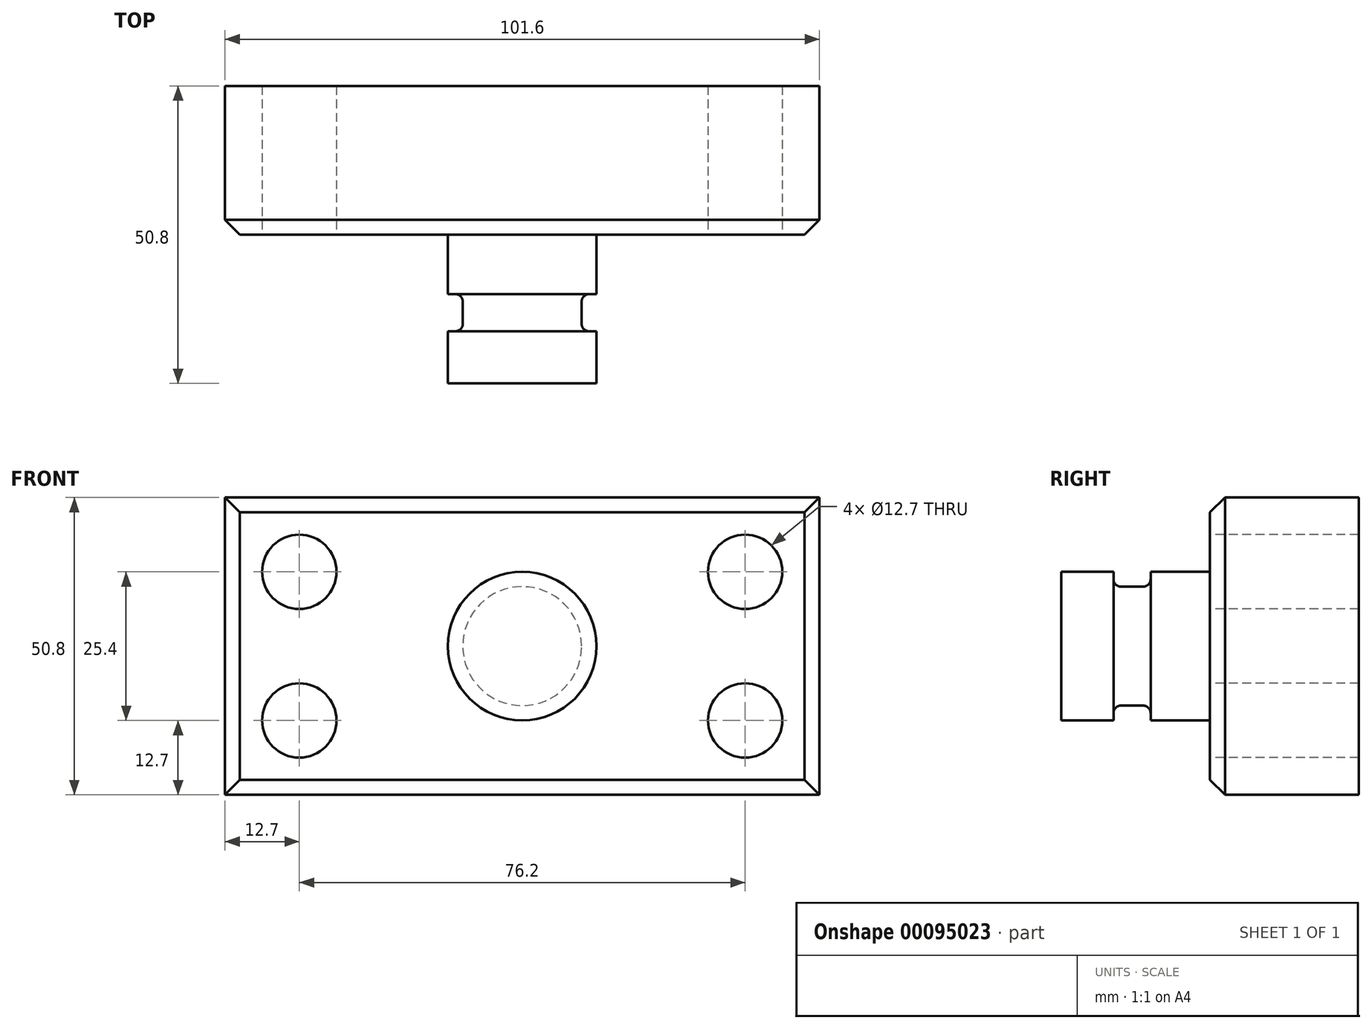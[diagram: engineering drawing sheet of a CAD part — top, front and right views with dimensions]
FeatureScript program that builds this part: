
annotation { "Feature Type Name" : "Feature", "Feature Type Description" : "" }
export const myFeature = defineFeature(function(context is Context, id is Id, definition is map)
    precondition{}
    {
        {
            var Q0;
            Q0=qCreatedBy(makeId("Front.planeOp"),FACE);
            var sketch = newSketch(context, id + "F0", { "sketchPlane" : qUnion([Q0])});
            skLineSegment(sketch, "E0.bottom", {"start": v(-50.8, 25.4) * mm, "end": v(50.8, 25.4) * mm});
            skLineSegment(sketch, "E0.top", {"start": v(-50.8, -25.4) * mm, "end": v(50.8, -25.4) * mm});
            skLineSegment(sketch, "E0.left", {"start": v(-50.8, 25.4) * mm, "end": v(-50.8, -25.4) * mm});
            skLineSegment(sketch, "E0.right", {"start": v(50.8, 25.4) * mm, "end": v(50.8, -25.4) * mm});
            skPoint(sketch, "E0.middle", {"position": v(0, 0) * mm});
            skSolve(sketch);
        }
        {
            var Q0;
            Q0 = qSketchRegion(id + "F0", true);
            extrude(context, id + "F1", {"entities" : qUnion([Q0]), "depth" : 25.4 * mm});
        }
        {
            var Q0;
            Q0=makeQuery(id+"F1.opExtrude","CAP_FACE",FACE,{"disambiguationData":[OSD([sQuery(id+"F0.wireOp",EDGE,"E0.bottom"),sQuery(id+"F0.wireOp",EDGE,"E0.top"),sQuery(id+"F0.wireOp",EDGE,"E0.left"),sQuery(id+"F0.wireOp",EDGE,"E0.right")])],"isStart":false});
            var sketch = newSketch(context, id + "F2", { "sketchPlane" : qUnion([Q0])});
            skCircle(sketch, "E1", {"center": v(-38.1, 12.7) * mm, "radius": 6.35 * mm});
            skCircle(sketch, "E2", {"center": v(-38.1, -12.7) * mm, "radius": 6.35 * mm});
            skCircle(sketch, "E3", {"center": v(38.1, 12.7) * mm, "radius": 6.35 * mm});
            skCircle(sketch, "E4", {"center": v(38.1, -12.7) * mm, "radius": 6.35 * mm});
            skSolve(sketch);
        }
        {
            var Q0;
            Q0=makeQuery(id+"F2.imprint","IMPRINT",FACE,{"disambiguationData":[TD([[makeQuery(id+"F2.imprint","IMPRINT",EDGE,{"derivedFrom":sQuery(id+"F2.wireOp",EDGE,"E1")}),1.0]])]});
            var Q1;
            Q1=makeQuery(id+"F2.imprint","IMPRINT",FACE,{"disambiguationData":[TD([[makeQuery(id+"F2.imprint","IMPRINT",EDGE,{"derivedFrom":sQuery(id+"F2.wireOp",EDGE,"E2")}),1.0]])]});
            var Q2;
            Q2=makeQuery(id+"F2.imprint","IMPRINT",FACE,{"disambiguationData":[TD([[makeQuery(id+"F2.imprint","IMPRINT",EDGE,{"derivedFrom":sQuery(id+"F2.wireOp",EDGE,"E3")}),1.0]])]});
            var Q3;
            Q3=makeQuery(id+"F2.imprint","IMPRINT",FACE,{"disambiguationData":[TD([[makeQuery(id+"F2.imprint","IMPRINT",EDGE,{"derivedFrom":sQuery(id+"F2.wireOp",EDGE,"E4")}),1.0]])]});
            extrude(context, id + "F3", {"entities" : qUnion([Q0, Q1, Q2, Q3]), "operationType" : NewBodyOperationType.REMOVE, "endBound" : BoundingType.THROUGH_ALL, "oppositeDirection" : true, "depth" : 25.4 * mm});
        }
        {
            var Q0;
            Q0=qCreatedBy(makeId("Top.planeOp"),FACE);
            var sketch = newSketch(context, id + "F4", { "sketchPlane" : qUnion([Q0])});
            skLineSegment(sketch, "E5.bottom", {"start": v(0, -25.4) * mm, "end": v(12.7, -25.4) * mm});
            skLineSegment(sketch, "E5.top", {"start": v(0, -50.8) * mm, "end": v(12.7, -50.8) * mm});
            skLineSegment(sketch, "E5.left", {"start": v(0, -25.4) * mm, "end": v(0, -50.8) * mm});
            skLineSegment(sketch, "E5.right", {"start": v(12.7, -25.4) * mm, "end": v(12.7, -50.8) * mm});
            skSolve(sketch);
        }
        {
            var Q0;
            Q0 = qSketchRegion(id + "F4", true);
            var Q1;
            Q1=sQuery(id+"F4.wireOp",EDGE,"E5.left");
            revolve(context, id + "F5", {"operationType" : NewBodyOperationType.ADD, "entities" : qUnion([Q0]), "axis" : qUnion([Q1]), "revolveType" : RevolveType.FULL});
        }
        {
            var Q0;
            Q0=qCreatedBy(makeId("Top.planeOp"),FACE);
            var sketch = newSketch(context, id + "F6", { "sketchPlane" : qUnion([Q0])});
            skLineSegment(sketch, "E6.bottom", {"start": v(17.8, -41.91) * mm, "end": v(10.16, -41.91) * mm});
            skLineSegment(sketch, "E6.top", {"start": v(17.8, -35.56) * mm, "end": v(10.16, -35.56) * mm});
            skLineSegment(sketch, "E6.left", {"start": v(17.8, -41.91) * mm, "end": v(17.8, -35.56) * mm});
            skLineSegment(sketch, "E6.right", {"start": v(10.16, -41.91) * mm, "end": v(10.16, -35.56) * mm});
            skLineSegment(sketch, "E7", {"start": v(0, 0) * mm, "end": v(0, -71.62) * mm, "construction": true});
            skSolve(sketch);
        }
        {
            var Q0;
            Q0 = qSketchRegion(id + "F6", true);
            var Q1;
            Q1=sQuery(id+"F6.wireOp",EDGE,"E7");
            revolve(context, id + "F7", {"operationType" : NewBodyOperationType.REMOVE, "entities" : qUnion([Q0]), "axis" : qUnion([Q1]), "revolveType" : RevolveType.FULL, "oppositeDirection" : true});
        }
        {
            var Q0;
            Q0=makeQuery(id+"F5.opRevolve","SWEPT_EDGE",EDGE,{"disambiguationData":[OSD([sQuery(id+"F4.wireOp",EDGE,"E5.bottom"),sQuery(id+"F4.wireOp",EDGE,"E5.right")])]});
            var Q1;
            Q1=makeQuery(id+"F7.boolean.opBoolean","COPY",EDGE,{"derivedFrom":makeQuery(id+"F7.opRevolve","SWEPT_EDGE",EDGE,{"disambiguationData":[OSD([sQuery(id+"F6.wireOp",EDGE,"E6.bottom"),sQuery(id+"F6.wireOp",EDGE,"E6.right")])]})});
            var Q2;
            Q2=makeQuery(id+"F7.boolean.opBoolean","COPY",EDGE,{"derivedFrom":makeQuery(id+"F7.opRevolve","SWEPT_EDGE",EDGE,{"disambiguationData":[OSD([sQuery(id+"F6.wireOp",EDGE,"E6.top"),sQuery(id+"F6.wireOp",EDGE,"E6.right")])]})});
            fillet(context, id + "F8", {"entities" : qUnion([Q0, Q1, Q2]), "radius" : 1.27 * mm, "tangentPropagation" : true, "allowEdgeOverflow" : false});
        }
        {
            var Q0;
            Q0=makeQuery(id+"F1.opExtrude","CAP_EDGE",EDGE,{"disambiguationData":[OSD([sQuery(id+"F0.wireOp",EDGE,"E0.bottom")])],"isStart":false});
            var Q1;
            Q1=makeQuery(id+"F1.opExtrude","CAP_EDGE",EDGE,{"disambiguationData":[OSD([sQuery(id+"F0.wireOp",EDGE,"E0.left")])],"isStart":false});
            var Q2;
            Q2=makeQuery(id+"F1.opExtrude","CAP_EDGE",EDGE,{"disambiguationData":[OSD([sQuery(id+"F0.wireOp",EDGE,"E0.top")])],"isStart":false});
            var Q3;
            Q3=makeQuery(id+"F1.opExtrude","CAP_EDGE",EDGE,{"disambiguationData":[OSD([sQuery(id+"F0.wireOp",EDGE,"E0.right")])],"isStart":false});
            chamfer(context, id + "F9", {"entities" : qUnion([Q0, Q1, Q2, Q3]), "width" : 2.54 * mm, "tangentPropagation" : true});
        }
    });
